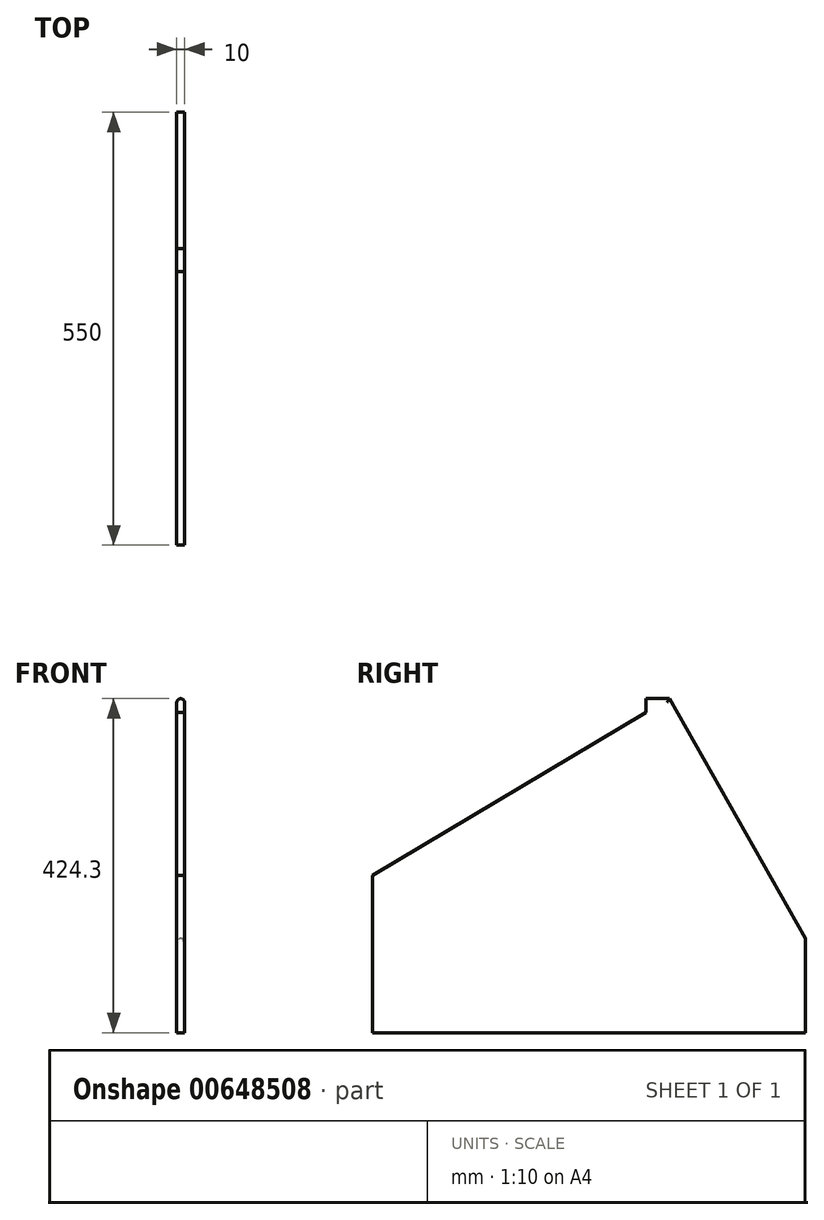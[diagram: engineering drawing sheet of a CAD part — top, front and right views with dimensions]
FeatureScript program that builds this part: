
annotation { "Feature Type Name" : "Feature", "Feature Type Description" : "" }
export const myFeature = defineFeature(function(context is Context, id is Id, definition is map)
    precondition{}
    {
        {
            var Q0;
            Q0=qCreatedBy(makeId("Right.planeOp"),FACE);
            var sketch = newSketch(context, id + "F0", { "sketchPlane" : qUnion([Q0])});
            skLineSegment(sketch, "E0", {"start": v(268.77, -74.31) * mm, "end": v(-281.23, -74.31) * mm});
            skLineSegment(sketch, "E1.bottom", {"start": v(-281.23, -74.31) * mm, "end": v(-174.2, -74.31) * mm});
            skLineSegment(sketch, "E1.top", {"start": v(-281.23, 125.69) * mm, "end": v(-174.2, 125.69) * mm});
            skLineSegment(sketch, "E1.left", {"start": v(-281.23, -74.31) * mm, "end": v(-281.23, 125.69) * mm});
            skLineSegment(sketch, "E1.right", {"start": v(-174.2, -74.31) * mm, "end": v(-174.2, 125.69) * mm});
            skLineSegment(sketch, "E2.bottom", {"start": v(268.77, -74.31) * mm, "end": v(155.05, -74.31) * mm});
            skLineSegment(sketch, "E2.top", {"start": v(268.77, 45.69) * mm, "end": v(155.05, 45.69) * mm});
            skLineSegment(sketch, "E2.left", {"start": v(268.77, -74.31) * mm, "end": v(268.77, 45.69) * mm});
            skLineSegment(sketch, "E2.right", {"start": v(155.05, -74.31) * mm, "end": v(155.05, 45.69) * mm});
            skLineSegment(sketch, "E3.bottom", {"start": v(66.1, -74.31) * mm, "end": v(95.85, -74.31) * mm});
            skLineSegment(sketch, "E3.top", {"start": v(66.1, 350) * mm, "end": v(95.85, 350) * mm});
            skLineSegment(sketch, "E3.left", {"start": v(66.1, -74.31) * mm, "end": v(66.1, 350) * mm});
            skLineSegment(sketch, "E3.right", {"start": v(95.85, -74.31) * mm, "end": v(95.85, 350) * mm});
            skLineSegment(sketch, "E4", {"start": v(268.77, 45.69) * mm, "end": v(95.85, 350) * mm});
            skLineSegment(sketch, "E5", {"start": v(95.85, 350) * mm, "end": v(-281.23, 125.69) * mm});
            skSolve(sketch);
        }
        {
            var Q0;
            Q0 = qSketchRegion(id + "F0", true);
            extrude(context, id + "F1", {"entities" : qUnion([Q0]), "depth" : 10 * mm, "offsetDistance" : 25 * mm});
        }
        {
            var Q0;
            Q0=makeQuery(id+"F1.opExtrude","CAP_EDGE",EDGE,{"disambiguationData":[OSD([sQuery(id+"F0.wireOp",EDGE,"E4")])],"isStart":false});
            var Q1;
            Q1=makeQuery(id+"F1.opExtrude","CAP_EDGE",EDGE,{"disambiguationData":[OSD([sQuery(id+"F0.wireOp",EDGE,"E4")])],"isStart":true});
            var Q2;
            Q2=makeQuery(id+"F1.opExtrude","CAP_EDGE",EDGE,{"disambiguationData":[OSD([sQuery(id+"F0.wireOp",EDGE,"E3.top")])],"isStart":false});
            var Q3;
            Q3=makeQuery(id+"F1.opExtrude","CAP_EDGE",EDGE,{"disambiguationData":[OSD([sQuery(id+"F0.wireOp",EDGE,"E3.top")])],"isStart":true});
            fillet(context, id + "F2", {"entities" : qUnion([Q0, Q1, Q2, Q3]), "radius" : 5 * mm, "tangentPropagation" : true, "allowEdgeOverflow" : false});
        }
    });
